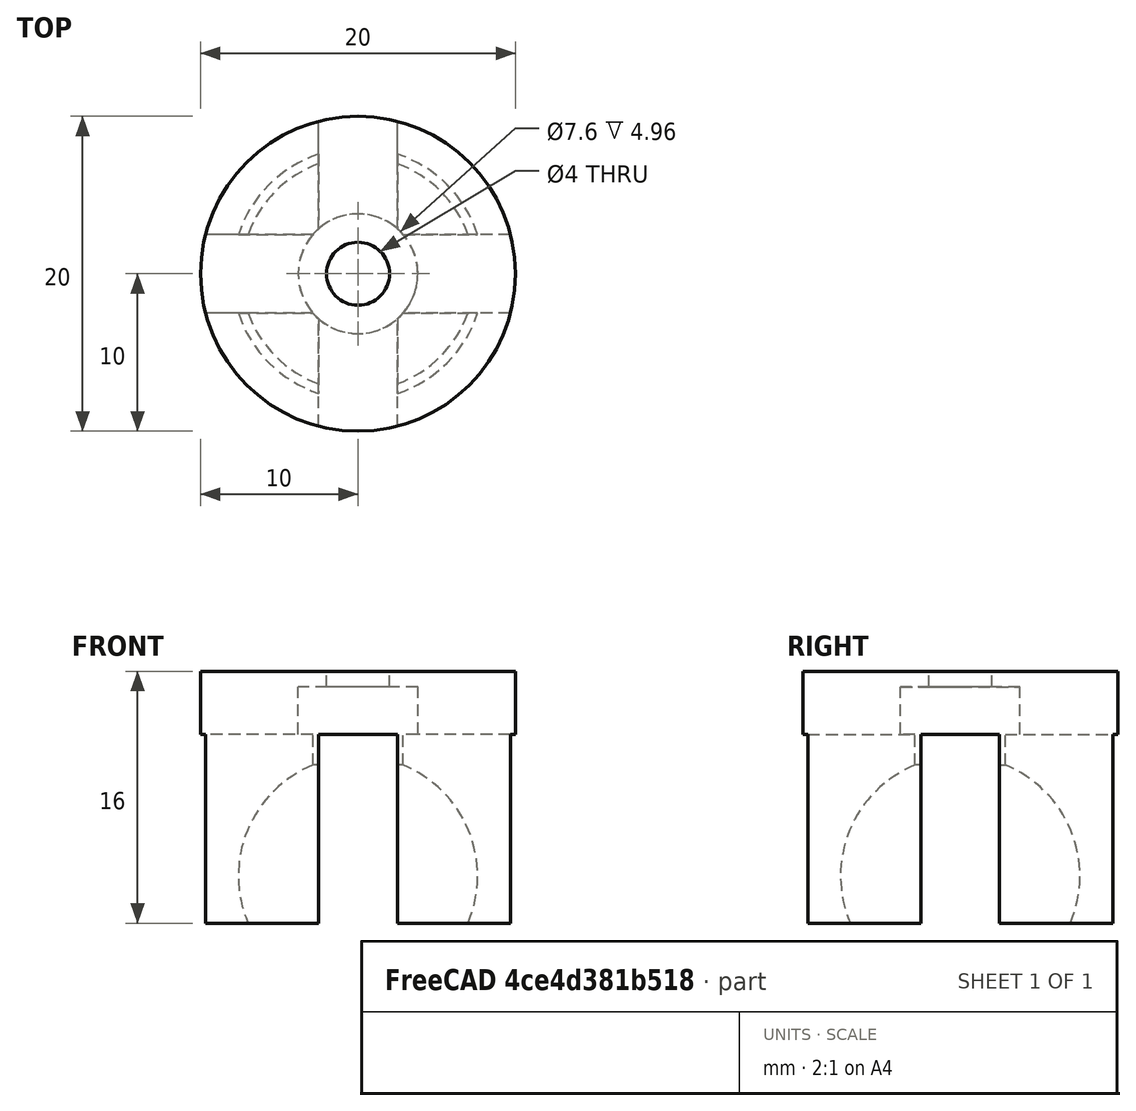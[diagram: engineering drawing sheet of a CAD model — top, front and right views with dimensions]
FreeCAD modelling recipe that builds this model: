
FCSTD DOCUMENT  (FreeCAD 0.16R6706 (Git))
Label: portabola
License: All rights reserved
LicenseURL: http://en.wikipedia.org/wiki/All_rights_reserved
objects: Part::Cylinder×3, Part::Cut×3, Part::Box×2, Part::MultiFuse×2, Part::Sphere×1
note: 11 computed .brp shape members not serialized (recipe doc carries the construction recipe); baked Part::Feature solids carry a one-line shape summary decoded from their .brp

FEATURE [Part::Cylinder] Cylinder  label="Cilindro"
  Angle = 360
  Height = 16
  Radius = 10
FEATURE [Part::Sphere] Sphere  label="Esfera"
  Angle1 = -90
  Angle2 = 90
  Angle3 = 360
  Placement = pos=(0,0,3) rot=(0,0,1;0rad)
  Radius = 8
FEATURE [Part::Cut] Cut
  Base = -> Cylinder
  Tool = -> Sphere
FEATURE [Part::Box] Box  label="Cubo"
  Height = 12
  Length = 5
  Placement = pos=(10,-2.5,0) rot=(0,0,1;1.5708rad)
  Width = 20
FEATURE [Part::Box] Box001  label="Cubo001"
  Height = 12
  Length = 5
  Placement = pos=(-2.5,-10,0) rot=(0,0,1;0rad)
  Width = 20
FEATURE [Part::MultiFuse] Fusion
  Shapes = -> [Box,Box001]
FEATURE [Part::Cut] Cut001
  Base = -> Cut
  Tool = -> Fusion
FEATURE [Part::Cylinder] Cylinder001  label="Cilindro001"
  Angle = 360
  Height = 16
  Radius = 2
FEATURE [Part::Cylinder] Cylinder002  label="Cilindro002"
  Angle = 360
  Height = 15
  Radius = 3.8
FEATURE [Part::MultiFuse] Fusion001
  Shapes = -> [Cylinder001,Cylinder002]
FEATURE [Part::Cut] Cut002
  Base = -> Cut001
  Tool = -> Fusion001
